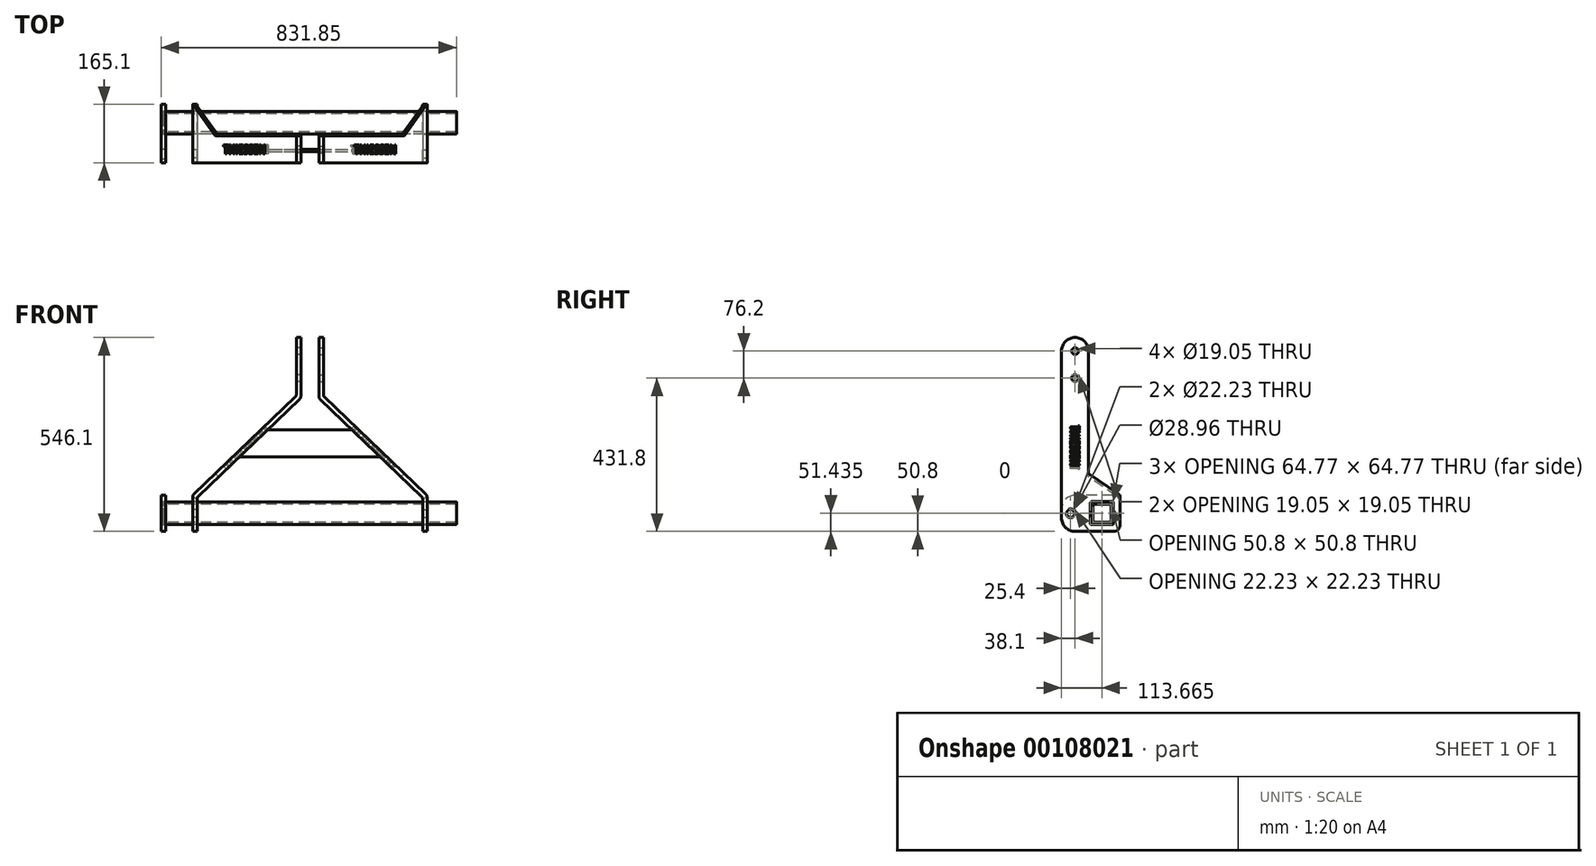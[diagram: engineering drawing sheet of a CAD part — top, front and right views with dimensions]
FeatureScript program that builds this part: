
annotation { "Feature Type Name" : "Feature", "Feature Type Description" : "" }
export const myFeature = defineFeature(function(context is Context, id is Id, definition is map)
    precondition{}
    {
        {
            var Q0;
            Q0=qCreatedBy(makeId("Front.planeOp"),FACE);
            var sketch = newSketch(context, id + "F0", { "sketchPlane" : qUnion([Q0])});
            skLineSegment(sketch, "E0", {"start": v(-330.2, 0) * mm, "end": v(-330.2, 101.6) * mm});
            skLineSegment(sketch, "E1", {"start": v(-330.2, 101.6) * mm, "end": v(-38.1, 381) * mm});
            skLineSegment(sketch, "E2", {"start": v(-38.1, 381) * mm, "end": v(-38.1, 546.1) * mm});
            skLineSegment(sketch, "E3", {"start": v(0, 0) * mm, "end": v(0, 360.93) * mm, "construction": true});
            skLineSegment(sketch, "E4.MirrorCS", {"start": v(38.1, 381) * mm, "end": v(38.1, 546.1) * mm});
            skLineSegment(sketch, "E5.MirrorCS", {"start": v(330.2, 101.6) * mm, "end": v(38.1, 381) * mm});
            skLineSegment(sketch, "E6.MirrorCS", {"start": v(330.2, 0) * mm, "end": v(330.2, 101.6) * mm});
            skSolve(sketch);
        }
        {
            var Q0;
            Q0=qCreatedBy(makeId("Top.planeOp"),FACE);
            var sketch = newSketch(context, id + "F1", { "sketchPlane" : qUnion([Q0])});
            skPoint(sketch, "E7.0", {"position": v(-330.2, 0) * mm});
            skPoint(sketch, "E7.1", {"position": v(330.2, 0) * mm});
            skLineSegment(sketch, "E8", {"start": v(-330.2, 38.1) * mm, "end": v(-330.2, -38.1) * mm});
            skLineSegment(sketch, "E9", {"start": v(0, 137.53) * mm, "end": v(0, -182.2) * mm, "construction": true});
            skLineSegment(sketch, "E10", {"start": v(-330.2, 38.1) * mm, "end": v(-317.5, 38.1) * mm});
            skLineSegment(sketch, "E11", {"start": v(-317.5, 38.1) * mm, "end": v(-317.5, -38.1) * mm});
            skLineSegment(sketch, "E12", {"start": v(-317.5, -38.1) * mm, "end": v(-330.2, -38.1) * mm});
            skSolve(sketch);
        }
        {
            var Q0;
            Q0=makeQuery(id+"F1.imprint","IMPRINT",FACE,{"disambiguationData":[TD([[makeQuery(id+"F1.imprint","IMPRINT",EDGE,{"derivedFrom":sQuery(id+"F1.wireOp",EDGE,"E8")}),1.0]])]});
            var Q1;
            Q1=sQuery(id+"F0.wireOp",EDGE,"E1");
            var Q2;
            Q2=sQuery(id+"F0.wireOp",EDGE,"E0");
            var Q3;
            Q3=sQuery(id+"F0.wireOp",EDGE,"E2");
            sweep(context, id + "F2", {"profiles" : qUnion([Q0]), "path" : qUnion([Q1, Q2, Q3])});
        }
        {
            var Q0;
            Q0=makeQuery(id+"F2.opSweep","SWEPT_FACE",FACE,{"disambiguationData":[OSD([sQuery(id+"F0.wireOp",EDGE,"E0"),sQuery(id+"F1.wireOp",EDGE,"E10")])]});
            var sketch = newSketch(context, id + "F3", { "sketchPlane" : qUnion([Q0])});
            skLineSegment(sketch, "E13.0", {"start": v(330.2, 101.6) * mm, "end": v(38.1, 381) * mm});
            skLineSegment(sketch, "E13.1", {"start": v(317.5, 96.17) * mm, "end": v(25.4, 375.57) * mm});
            skLineSegment(sketch, "E13.2", {"start": v(330.2, 0) * mm, "end": v(330.2, 101.6) * mm});
            skLineSegment(sketch, "E13.3", {"start": v(317.5, 0) * mm, "end": v(317.5, 96.17) * mm});
            skLineSegment(sketch, "E13.4", {"start": v(317.5, 0) * mm, "end": v(330.2, 0) * mm});
            skLineSegment(sketch, "E14", {"start": v(265.96, 163.05) * mm, "end": v(257.18, 153.87) * mm});
            skSolve(sketch);
        }
        {
            var Q0;
            {var subQ0=sQuery(id+"F3.wireOp",EDGE,"E13.2");Q0=makeQuery(id+"F3.imprint","IMPRINT",FACE,{"disambiguationData":[TD([[makeQuery(id+"F3.imprint","IMPRINT",EDGE,{"derivedFrom":subQ0}),1.0]])]});}
            extrude(context, id + "F4", {"entities" : qUnion([Q0]), "operationType" : NewBodyOperationType.ADD, "depth" : 88.9 * mm});
        }
        {
            var Q0;
            Q0=makeQuery(id+"F4.boolean.opBoolean","MERGE",FACE,{"derivedFrom":[makeQuery(id+"F2.opSweep","SWEPT_FACE",FACE,{"disambiguationData":[OSD([sQuery(id+"F0.wireOp",EDGE,"E1"),sQuery(id+"F1.wireOp",EDGE,"E8")])]}),makeQuery(id+"F4.opExtrude","SWEPT_FACE",FACE,{"disambiguationData":[OSD([sQuery(id+"F3.wireOp",EDGE,"E13.0")])]})]});
            var sketch = newSketch(context, id + "F5", { "sketchPlane" : qUnion([Q0])});
            skLineSegment(sketch, "E15.0", {"start": v(-79.49, 127) * mm, "end": v(-79.49, 38.1) * mm});
            skLineSegment(sketch, "E15.1", {"start": v(-168.39, 127) * mm, "end": v(-79.49, 127) * mm});
            skLineSegment(sketch, "E16", {"start": v(-79.49, 38.1) * mm, "end": v(-168.39, 127) * mm});
            skSolve(sketch);
        }
        {
            var Q0;
            Q0 = qSketchRegion(id + "F5", true);
            var Q1;
            Q1=makeQuery(id+"F4.boolean.opBoolean","MERGE",FACE,{"derivedFrom":[makeQuery(id+"F2.opSweep","SWEPT_FACE",FACE,{"disambiguationData":[OSD([sQuery(id+"F0.wireOp",EDGE,"E1"),sQuery(id+"F1.wireOp",EDGE,"E11")])]}),makeQuery(id+"F4.opExtrude","SWEPT_FACE",FACE,{"disambiguationData":[OSD([sQuery(id+"F3.wireOp",EDGE,"E13.1")])]})]});
            extrude(context, id + "F6", {"entities" : qUnion([Q0]), "operationType" : NewBodyOperationType.REMOVE, "endBound" : BoundingType.THROUGH_ALL, "oppositeDirection" : true, "endBoundEntityFace" : qUnion([Q1]), "depth" : 25.4 * mm});
        }
        {
            var Q0;
            Q0=makeQuery(id+"F2.opSweep","MID_CAP_EDGE",EDGE,{"disambiguationData":[OSD([sQuery(id+"F0.wireOp",VERTEX,"E0.end"),sQuery(id+"F1.wireOp",EDGE,"E8")])],"capPos":1.0});
            var Q1;
            Q1=makeQuery(id+"F2.opSweep","MID_CAP_EDGE",EDGE,{"disambiguationData":[OSD([sQuery(id+"F0.wireOp",VERTEX,"E0.end"),sQuery(id+"F1.wireOp",EDGE,"E11")])],"capPos":1.0});
            var Q2;
            Q2=makeQuery(id+"F2.opSweep","MID_CAP_EDGE",EDGE,{"disambiguationData":[OSD([sQuery(id+"F0.wireOp",VERTEX,"E2.start"),sQuery(id+"F1.wireOp",EDGE,"E8")])],"capPos":2.0});
            var Q3;
            Q3=makeQuery(id+"F2.opSweep","MID_CAP_EDGE",EDGE,{"disambiguationData":[OSD([sQuery(id+"F0.wireOp",VERTEX,"E2.start"),sQuery(id+"F1.wireOp",EDGE,"E11")])],"capPos":2.0});
            fillet(context, id + "F7", {"entities" : qUnion([Q0, Q1, Q2, Q3]), "radius" : 12.7 * mm, "tangentPropagation" : true, "allowEdgeOverflow" : false});
        }
        {
            var Q0;
            Q0=makeQuery(id+"F2.opSweep","CAP_EDGE",EDGE,{"disambiguationData":[OSD([sQuery(id+"F0.wireOp",VERTEX,"E2.end"),sQuery(id+"F1.wireOp",EDGE,"E12")])],"isStart":false});
            var Q1;
            Q1=makeQuery(id+"F2.opSweep","CAP_EDGE",EDGE,{"disambiguationData":[OSD([sQuery(id+"F0.wireOp",VERTEX,"E2.end"),sQuery(id+"F1.wireOp",EDGE,"E10")])],"isStart":false});
            var Q2;
            Q2=makeQuery(id+"F2.opSweep","CAP_EDGE",EDGE,{"disambiguationData":[OSD([sQuery(id+"F0.wireOp",VERTEX,"E0.start"),sQuery(id+"F1.wireOp",EDGE,"E12")])],"isStart":true});
            fillet(context, id + "F8", {"entities" : qUnion([Q0, Q1, Q2]), "radius" : 38.1 * mm, "tangentPropagation" : true, "allowEdgeOverflow" : false});
        }
        {
            var Q0;
            Q0=makeQuery(id+"F2.opSweep","SWEPT_FACE",FACE,{"disambiguationData":[OSD([sQuery(id+"F0.wireOp",EDGE,"E2"),sQuery(id+"F1.wireOp",EDGE,"E8")])]});
            var sketch = newSketch(context, id + "F9", { "sketchPlane" : qUnion([Q0])});
            skPoint(sketch, "E17.0", {"position": v(0, 546.1) * mm});
            skPoint(sketch, "E17.1", {"position": v(0, 381) * mm});
            skCircle(sketch, "E18", {"center": v(0, 508) * mm, "radius": 9.53 * mm});
            skCircle(sketch, "E19", {"center": v(0, 431.8) * mm, "radius": 9.53 * mm});
            skSolve(sketch);
        }
        {
            var Q0;
            Q0=makeQuery(id+"F9.imprint","IMPRINT",FACE,{"disambiguationData":[TD([[makeQuery(id+"F9.imprint","IMPRINT",EDGE,{"derivedFrom":sQuery(id+"F9.wireOp",EDGE,"E18")}),1.0]])]});
            var Q1;
            Q1=makeQuery(id+"F9.imprint","IMPRINT",FACE,{"disambiguationData":[TD([[makeQuery(id+"F9.imprint","IMPRINT",EDGE,{"derivedFrom":sQuery(id+"F9.wireOp",EDGE,"E19")}),1.0]])]});
            var Q2;
            Q2=makeQuery(id+"F2.opSweep","SWEPT_FACE",FACE,{"disambiguationData":[OSD([sQuery(id+"F0.wireOp",EDGE,"E2"),sQuery(id+"F1.wireOp",EDGE,"E11")])]});
            extrude(context, id + "F10", {"entities" : qUnion([Q0, Q1]), "operationType" : NewBodyOperationType.REMOVE, "endBound" : BoundingType.UP_TO_SURFACE, "oppositeDirection" : true, "endBoundEntityFace" : qUnion([Q2]), "depth" : 25.4 * mm});
        }
        {
            var Q0;
            Q0=makeQuery(id+"F2.opSweep","SWEPT_FACE",FACE,{"disambiguationData":[OSD([sQuery(id+"F0.wireOp",EDGE,"E0"),sQuery(id+"F1.wireOp",EDGE,"E8")])]});
            var sketch = newSketch(context, id + "F11", { "sketchPlane" : qUnion([Q0])});
            skPoint(sketch, "E20.0", {"position": v(0, 101.6) * mm});
            skPoint(sketch, "E20.1", {"position": v(0, 0) * mm});
            skCircle(sketch, "E21", {"center": v(12.7, 50.8) * mm, "radius": 11.11 * mm});
            skLineSegment(sketch, "E22.0", {"start": v(38.1, 38.1) * mm, "end": v(38.1, 96.17) * mm});
            skSolve(sketch);
        }
        {
            var Q0;
            Q0=makeQuery(id+"F11.imprint","IMPRINT",FACE,{"disambiguationData":[TD([[makeQuery(id+"F11.imprint","IMPRINT",EDGE,{"derivedFrom":sQuery(id+"F11.wireOp",EDGE,"E21")}),1.0]])]});
            var Q1;
            Q1=makeQuery(id+"F2.opSweep","SWEPT_FACE",FACE,{"disambiguationData":[OSD([sQuery(id+"F0.wireOp",EDGE,"E0"),sQuery(id+"F1.wireOp",EDGE,"E11")])]});
            extrude(context, id + "F12", {"entities" : qUnion([Q0]), "operationType" : NewBodyOperationType.REMOVE, "endBound" : BoundingType.UP_TO_SURFACE, "oppositeDirection" : true, "endBoundEntityFace" : qUnion([Q1]), "depth" : 25.4 * mm});
        }
        {
            var Q0;
            Q0=makeQuery(id+"F4.opExtrude","CAP_EDGE",EDGE,{"disambiguationData":[OSD([sQuery(id+"F3.wireOp",EDGE,"E13.4")])],"isStart":false});
            var Q1;
            Q1=makeQuery(id+"F6.boolean.opBoolean","COPY",EDGE,{"derivedFrom":makeQuery(id+"F6.opExtrude","SWEPT_EDGE",EDGE,{"disambiguationData":[OSD([sQuery(id+"F0.wireOp",VERTEX,"E0.end"),sQuery(id+"F1.wireOp",EDGE,"E8"),sQuery(id+"F3.wireOp",EDGE,"E13.0"),sQuery(id+"F3.wireOp",EDGE,"E13.2"),sQuery(id+"F5.wireOp",EDGE,"E15.1"),sQuery(id+"F5.wireOp",EDGE,"E16")])]})});
            var Q2;
            Q2=makeQuery(id+"F6.boolean.opBoolean","MERGE",EDGE,{"derivedFrom":[makeQuery(id+"F4.opExtrude","CAP_EDGE",EDGE,{"disambiguationData":[OSD([sQuery(id+"F3.wireOp",EDGE,"E14")])],"isStart":true}),makeQuery(id+"F6.opExtrude","SWEPT_EDGE",EDGE,{"disambiguationData":[OSD([sQuery(id+"F0.wireOp",EDGE,"E1"),sQuery(id+"F1.wireOp",EDGE,"E8"),sQuery(id+"F1.wireOp",EDGE,"E10"),sQuery(id+"F5.wireOp",EDGE,"E15.0"),sQuery(id+"F5.wireOp",EDGE,"E16")])]})]});
            fillet(context, id + "F13", {"entities" : qUnion([Q0, Q1, Q2]), "radius" : 19.05 * mm, "tangentPropagation" : true, "allowEdgeOverflow" : false});
        }
        {
            var Q0;
            Q0=makeQuery(id+"F4.boolean.opBoolean","MERGE",FACE,{"derivedFrom":[makeQuery(id+"F2.opSweep","SWEPT_FACE",FACE,{"disambiguationData":[OSD([sQuery(id+"F0.wireOp",EDGE,"E0"),sQuery(id+"F1.wireOp",EDGE,"E8")])]}),makeQuery(id+"F4.opExtrude","SWEPT_FACE",FACE,{"disambiguationData":[OSD([sQuery(id+"F3.wireOp",EDGE,"E13.2")])]})]});
            var sketch = newSketch(context, id + "F14", { "sketchPlane" : qUnion([Q0])});
            skLineSegment(sketch, "E23.0", {"start": v(-127, 19.05) * mm, "end": v(-127, 90.18) * mm});
            skLineSegment(sketch, "E23.1", {"start": v(-107.95, 0) * mm, "end": v(0, 0) * mm});
            skLineSegment(sketch, "E24", {"start": v(-107.95, 83.82) * mm, "end": v(-107.95, 19.05) * mm});
            skLineSegment(sketch, "E25", {"start": v(-107.95, 19.05) * mm, "end": v(-43.18, 19.05) * mm});
            skLineSegment(sketch, "E26", {"start": v(-43.18, 19.05) * mm, "end": v(-43.18, 83.82) * mm});
            skLineSegment(sketch, "E27", {"start": v(-43.18, 83.82) * mm, "end": v(-107.95, 83.82) * mm});
            skSolve(sketch);
        }
        {
            var Q0;
            Q0 = qSketchRegion(id + "F14", true);
            var Q1;
            Q1=makeQuery(id+"F4.boolean.opBoolean","MERGE",FACE,{"derivedFrom":[makeQuery(id+"F2.opSweep","SWEPT_FACE",FACE,{"disambiguationData":[OSD([sQuery(id+"F0.wireOp",EDGE,"E0"),sQuery(id+"F1.wireOp",EDGE,"E11")])]}),makeQuery(id+"F4.opExtrude","SWEPT_FACE",FACE,{"disambiguationData":[OSD([sQuery(id+"F3.wireOp",EDGE,"E13.3")])]})]});
            extrude(context, id + "F15", {"entities" : qUnion([Q0]), "operationType" : NewBodyOperationType.REMOVE, "endBound" : BoundingType.UP_TO_SURFACE, "oppositeDirection" : true, "endBoundEntityFace" : qUnion([Q1]), "depth" : 25.4 * mm});
        }
        {
            var Q0;
            Q0=makeQuery(id+"F15.boolean.opBoolean","COPY",EDGE,{"derivedFrom":makeQuery(id+"F15.opExtrude","SWEPT_EDGE",EDGE,{"disambiguationData":[OSD([sQuery(id+"F14.wireOp",EDGE,"E24"),sQuery(id+"F14.wireOp",EDGE,"E27")])]})});
            var Q1;
            Q1=makeQuery(id+"F15.boolean.opBoolean","COPY",EDGE,{"derivedFrom":makeQuery(id+"F15.opExtrude","SWEPT_EDGE",EDGE,{"disambiguationData":[OSD([sQuery(id+"F14.wireOp",EDGE,"E26"),sQuery(id+"F14.wireOp",EDGE,"E27")])]})});
            var Q2;
            Q2=makeQuery(id+"F15.boolean.opBoolean","COPY",EDGE,{"derivedFrom":makeQuery(id+"F15.opExtrude","SWEPT_EDGE",EDGE,{"disambiguationData":[OSD([sQuery(id+"F14.wireOp",EDGE,"E25"),sQuery(id+"F14.wireOp",EDGE,"E26")])]})});
            var Q3;
            Q3=makeQuery(id+"F15.boolean.opBoolean","COPY",EDGE,{"derivedFrom":makeQuery(id+"F15.opExtrude","SWEPT_EDGE",EDGE,{"disambiguationData":[OSD([sQuery(id+"F14.wireOp",EDGE,"E24"),sQuery(id+"F14.wireOp",EDGE,"E25")])]})});
            fillet(context, id + "F16", {"entities" : qUnion([Q0, Q1, Q2, Q3]), "radius" : 3.17 * mm, "tangentPropagation" : true, "allowEdgeOverflow" : false});
        }
        {
            var Q0;
            Q0=makeQuery(id+"F2.opSweep","SWEPT_BODY",BODY,{"disambiguationData":[OSD([sQuery(id+"F0.wireOp",EDGE,"E0"),sQuery(id+"F1.wireOp",EDGE,"E8"),sQuery(id+"F1.wireOp",EDGE,"E10"),sQuery(id+"F1.wireOp",EDGE,"E11"),sQuery(id+"F1.wireOp",EDGE,"E12")])]});
            var Q1;
            Q1=qCreatedBy(makeId("Right.planeOp"),FACE);
            mirror(context, id + "F17", {"entities" : qUnion([Q0]), "mirrorPlane" : qUnion([Q1])});
        }
        {
            var Q0;
            Q0=qCreatedBy(makeId("Right.planeOp"),FACE);
            var sketch = newSketch(context, id + "F18", { "sketchPlane" : qUnion([Q0])});
            skLineSegment(sketch, "E28.0", {"start": v(46.35, 83.82) * mm, "end": v(104.77, 83.82) * mm, "construction": true});
            skLineSegment(sketch, "E28.1", {"start": v(107.95, 80.65) * mm, "end": v(107.95, 22.22) * mm, "construction": true});
            skLineSegment(sketch, "E28.2", {"start": v(104.77, 19.05) * mm, "end": v(46.35, 19.05) * mm, "construction": true});
            skLineSegment(sketch, "E28.3", {"start": v(43.18, 22.22) * mm, "end": v(43.18, 80.65) * mm, "construction": true});
            skLineSegment(sketch, "E29", {"start": v(75.56, 83.82) * mm, "end": v(75.56, 19.05) * mm, "construction": true});
            skLineSegment(sketch, "E30", {"start": v(107.95, 51.44) * mm, "end": v(43.18, 51.44) * mm, "construction": true});
            skLineSegment(sketch, "E31", {"start": v(107.32, 83.19) * mm, "end": v(43.81, 83.19) * mm});
            skLineSegment(sketch, "E32", {"start": v(43.81, 83.19) * mm, "end": v(43.81, 19.69) * mm});
            skLineSegment(sketch, "E33", {"start": v(43.81, 19.69) * mm, "end": v(107.31, 19.69) * mm});
            skLineSegment(sketch, "E34", {"start": v(107.31, 19.69) * mm, "end": v(107.31, 83.18) * mm});
            skLineSegment(sketch, "E35", {"start": v(100.96, 76.84) * mm, "end": v(50.16, 76.84) * mm});
            skLineSegment(sketch, "E36", {"start": v(50.16, 76.84) * mm, "end": v(50.16, 26.04) * mm});
            skLineSegment(sketch, "E37", {"start": v(50.16, 26.04) * mm, "end": v(100.96, 26.04) * mm});
            skLineSegment(sketch, "E38", {"start": v(100.96, 26.04) * mm, "end": v(100.96, 76.84) * mm});
            skSolve(sketch);
        }
        {
            var Q0;
            Q0=makeQuery(id+"F18.imprint","IMPRINT",FACE,{"disambiguationData":[TD([[makeQuery(id+"F18.imprint","IMPRINT",EDGE,{"derivedFrom":sQuery(id+"F18.wireOp",EDGE,"E31")}),1.0]])]});
            extrude(context, id + "F19", {"entities" : qUnion([Q0]), "endBound" : BoundingType.SYMMETRIC, "depth" : 825.5 * mm});
        }
        {
            var Q0;
            Q0=makeQuery(id+"F19.opExtrude","SWEPT_EDGE",EDGE,{"disambiguationData":[OSD([sQuery(id+"F18.wireOp",EDGE,"E35"),sQuery(id+"F18.wireOp",EDGE,"E38")])]});
            var Q1;
            Q1=makeQuery(id+"F19.opExtrude","SWEPT_EDGE",EDGE,{"disambiguationData":[OSD([sQuery(id+"F18.wireOp",EDGE,"E35"),sQuery(id+"F18.wireOp",EDGE,"E36")])]});
            var Q2;
            Q2=makeQuery(id+"F19.opExtrude","SWEPT_EDGE",EDGE,{"disambiguationData":[OSD([sQuery(id+"F18.wireOp",EDGE,"E36"),sQuery(id+"F18.wireOp",EDGE,"E37")])]});
            var Q3;
            Q3=makeQuery(id+"F19.opExtrude","SWEPT_EDGE",EDGE,{"disambiguationData":[OSD([sQuery(id+"F18.wireOp",EDGE,"E37"),sQuery(id+"F18.wireOp",EDGE,"E38")])]});
            var Q4;
            Q4=makeQuery(id+"F19.opExtrude","SWEPT_EDGE",EDGE,{"disambiguationData":[OSD([sQuery(id+"F18.wireOp",EDGE,"E31"),sQuery(id+"F18.wireOp",EDGE,"E32")])]});
            var Q5;
            Q5=makeQuery(id+"F19.opExtrude","SWEPT_EDGE",EDGE,{"disambiguationData":[OSD([sQuery(id+"F18.wireOp",EDGE,"E32"),sQuery(id+"F18.wireOp",EDGE,"E33")])]});
            var Q6;
            Q6=makeQuery(id+"F19.opExtrude","SWEPT_EDGE",EDGE,{"disambiguationData":[OSD([sQuery(id+"F18.wireOp",EDGE,"E33"),sQuery(id+"F18.wireOp",EDGE,"E34")])]});
            var Q7;
            Q7=makeQuery(id+"F19.opExtrude","SWEPT_EDGE",EDGE,{"disambiguationData":[OSD([sQuery(id+"F18.wireOp",EDGE,"E31"),sQuery(id+"F18.wireOp",EDGE,"E34")])]});
            fillet(context, id + "F20", {"entities" : qUnion([Q0, Q1, Q2, Q3, Q4, Q5, Q6, Q7]), "radius" : 6.35 * mm, "tangentPropagation" : true, "allowEdgeOverflow" : false});
        }
        {
            var Q0;
            Q0=makeQuery(id+"F4.boolean.opBoolean","MERGE",FACE,{"derivedFrom":[makeQuery(id+"F2.opSweep","SWEPT_FACE",FACE,{"disambiguationData":[OSD([sQuery(id+"F0.wireOp",EDGE,"E1"),sQuery(id+"F1.wireOp",EDGE,"E8")])]}),makeQuery(id+"F4.opExtrude","SWEPT_FACE",FACE,{"disambiguationData":[OSD([sQuery(id+"F3.wireOp",EDGE,"E13.0")])]})]});
            var sketch = newSketch(context, id + "F21", { "sketchPlane" : qUnion([Q0])});
            skText(sketch, "E39", { "text": "THIESSEN", "fontName": "OpenSans-Bold.ttf"});
            skLineSegment(sketch, "E40.0", {"start": v(230.4, -38.1) * mm, "end": v(230.4, 38.1) * mm});
            skLineSegment(sketch, "E40.1", {"start": v(-162.96, 121.57) * mm, "end": v(-162.96, -38.1) * mm});
            skLineSegment(sketch, "E40.2", {"start": v(-71.6, 38.1) * mm, "end": v(230.4, 38.1) * mm});
            skLineSegment(sketch, "E40.3", {"start": v(-162.96, -38.1) * mm, "end": v(230.4, -38.1) * mm});
            skLineSegment(sketch, "E41", {"start": v(230.4, 0) * mm, "end": v(-162.96, 0) * mm, "construction": true});
            skLineSegment(sketch, "E42", {"start": v(33.72, -38.1) * mm, "end": v(33.72, 38.1) * mm, "construction": true});
            const initialGuessF21  = {"E39": [-0.04892, -0.0127, 1, 0, 0.0254]};
            skSetInitialGuess(sketch, initialGuessF21);
            skSolve(sketch);
        }
        {
            var Q0;
            Q0=makeQuery(id+"F21.imprint","IMPRINT",FACE,{"disambiguationData":[TD([[makeQuery(id+"F21.imprint","IMPRINT",EDGE,{"derivedFrom":sQuery(id+"F21.wireOp",EDGE,"E39.sketch_text.stroke-104")}),-1.0]])]});
            var Q1;
            Q1=makeQuery(id+"F21.imprint","IMPRINT",FACE,{"disambiguationData":[TD([[makeQuery(id+"F21.imprint","IMPRINT",EDGE,{"derivedFrom":sQuery(id+"F21.wireOp",EDGE,"E39.sketch_text.stroke-92")}),-1.0]])]});
            var Q2;
            Q2=makeQuery(id+"F21.imprint","IMPRINT",FACE,{"disambiguationData":[TD([[makeQuery(id+"F21.imprint","IMPRINT",EDGE,{"derivedFrom":sQuery(id+"F21.wireOp",EDGE,"E39.sketch_text.stroke-64")}),-1.0]])]});
            var Q3;
            Q3=makeQuery(id+"F21.imprint","IMPRINT",FACE,{"disambiguationData":[TD([[makeQuery(id+"F21.imprint","IMPRINT",EDGE,{"derivedFrom":sQuery(id+"F21.wireOp",EDGE,"E39.sketch_text.stroke-36")}),-1.0]])]});
            var Q4;
            Q4=makeQuery(id+"F21.imprint","IMPRINT",FACE,{"disambiguationData":[TD([[makeQuery(id+"F21.imprint","IMPRINT",EDGE,{"derivedFrom":sQuery(id+"F21.wireOp",EDGE,"E39.sketch_text.stroke-24")}),-1.0]])]});
            var Q5;
            Q5=makeQuery(id+"F21.imprint","IMPRINT",FACE,{"disambiguationData":[TD([[makeQuery(id+"F21.imprint","IMPRINT",EDGE,{"derivedFrom":sQuery(id+"F21.wireOp",EDGE,"E39.sketch_text.stroke-20")}),-1.0]])]});
            var Q6;
            Q6=makeQuery(id+"F21.imprint","IMPRINT",FACE,{"disambiguationData":[TD([[makeQuery(id+"F21.imprint","IMPRINT",EDGE,{"derivedFrom":sQuery(id+"F21.wireOp",EDGE,"E39.sketch_text.stroke-8")}),-1.0]])]});
            var Q7;
            Q7=makeQuery(id+"F21.imprint","IMPRINT",FACE,{"disambiguationData":[TD([[makeQuery(id+"F21.imprint","IMPRINT",EDGE,{"derivedFrom":sQuery(id+"F21.wireOp",EDGE,"E39.sketch_text.stroke-0")}),-1.0]])]});
            var Q8;
            Q8=makeQuery(id+"F4.boolean.opBoolean","MERGE",FACE,{"derivedFrom":[makeQuery(id+"F2.opSweep","SWEPT_FACE",FACE,{"disambiguationData":[OSD([sQuery(id+"F0.wireOp",EDGE,"E1"),sQuery(id+"F1.wireOp",EDGE,"E11")])]}),makeQuery(id+"F4.opExtrude","SWEPT_FACE",FACE,{"disambiguationData":[OSD([sQuery(id+"F3.wireOp",EDGE,"E13.1")])]})]});
            extrude(context, id + "F22", {"entities" : qUnion([Q0, Q1, Q2, Q3, Q4, Q5, Q6, Q7]), "operationType" : NewBodyOperationType.REMOVE, "endBound" : BoundingType.UP_TO_SURFACE, "oppositeDirection" : true, "endBoundEntityFace" : qUnion([Q8]), "depth" : 25.4 * mm});
        }
        {
            var Q0;
            Q0=makeQuery(id+"F17.opPattern","COPY",FACE,{"derivedFrom":makeQuery(id+"F4.boolean.opBoolean","MERGE",FACE,{"derivedFrom":[makeQuery(id+"F2.opSweep","SWEPT_FACE",FACE,{"disambiguationData":[OSD([sQuery(id+"F0.wireOp",EDGE,"E1"),sQuery(id+"F1.wireOp",EDGE,"E8")])]}),makeQuery(id+"F4.opExtrude","SWEPT_FACE",FACE,{"disambiguationData":[OSD([sQuery(id+"F3.wireOp",EDGE,"E13.0")])]})]}),"instanceName":"1"});
            var sketch = newSketch(context, id + "F23", { "sketchPlane" : qUnion([Q0])});
            skLineSegment(sketch, "E43.0", {"start": v(-230.4, -38.1) * mm, "end": v(-230.4, 38.1) * mm});
            skLineSegment(sketch, "E43.1", {"start": v(162.96, 121.57) * mm, "end": v(162.96, -38.1) * mm});
            skLineSegment(sketch, "E43.2", {"start": v(162.96, -38.1) * mm, "end": v(-230.4, -38.1) * mm});
            skLineSegment(sketch, "E43.3", {"start": v(71.6, 38.1) * mm, "end": v(-230.4, 38.1) * mm});
            skText(sketch, "E44", { "text": "THIESSEN", "fontName": "OpenSans-Bold.ttf"});
            skLineSegment(sketch, "E45", {"start": v(-230.4, 0) * mm, "end": v(162.96, 0) * mm, "construction": true});
            skLineSegment(sketch, "E46", {"start": v(-33.72, -38.1) * mm, "end": v(-33.72, 38.1) * mm, "construction": true});
            const initialGuessF23  = {"E44": [-0.11635, -0.0127, 1, 0, 0.0254]};
            skSetInitialGuess(sketch, initialGuessF23);
            skSolve(sketch);
        }
        {
            var Q0;
            Q0=makeQuery(id+"F23.imprint","IMPRINT",FACE,{"disambiguationData":[TD([[makeQuery(id+"F23.imprint","IMPRINT",EDGE,{"derivedFrom":sQuery(id+"F23.wireOp",EDGE,"E44.sketch_text.stroke-0")}),-1.0]])]});
            var Q1;
            Q1=makeQuery(id+"F23.imprint","IMPRINT",FACE,{"disambiguationData":[TD([[makeQuery(id+"F23.imprint","IMPRINT",EDGE,{"derivedFrom":sQuery(id+"F23.wireOp",EDGE,"E44.sketch_text.stroke-8")}),-1.0]])]});
            var Q2;
            Q2=makeQuery(id+"F23.imprint","IMPRINT",FACE,{"disambiguationData":[TD([[makeQuery(id+"F23.imprint","IMPRINT",EDGE,{"derivedFrom":sQuery(id+"F23.wireOp",EDGE,"E44.sketch_text.stroke-20")}),-1.0]])]});
            var Q3;
            Q3=makeQuery(id+"F23.imprint","IMPRINT",FACE,{"disambiguationData":[TD([[makeQuery(id+"F23.imprint","IMPRINT",EDGE,{"derivedFrom":sQuery(id+"F23.wireOp",EDGE,"E44.sketch_text.stroke-24")}),-1.0]])]});
            var Q4;
            Q4=makeQuery(id+"F23.imprint","IMPRINT",FACE,{"disambiguationData":[TD([[makeQuery(id+"F23.imprint","IMPRINT",EDGE,{"derivedFrom":sQuery(id+"F23.wireOp",EDGE,"E44.sketch_text.stroke-36")}),-1.0]])]});
            var Q5;
            Q5=makeQuery(id+"F23.imprint","IMPRINT",FACE,{"disambiguationData":[TD([[makeQuery(id+"F23.imprint","IMPRINT",EDGE,{"derivedFrom":sQuery(id+"F23.wireOp",EDGE,"E44.sketch_text.stroke-64")}),-1.0]])]});
            var Q6;
            Q6=makeQuery(id+"F23.imprint","IMPRINT",FACE,{"disambiguationData":[TD([[makeQuery(id+"F23.imprint","IMPRINT",EDGE,{"derivedFrom":sQuery(id+"F23.wireOp",EDGE,"E44.sketch_text.stroke-92")}),-1.0]])]});
            var Q7;
            Q7=makeQuery(id+"F23.imprint","IMPRINT",FACE,{"disambiguationData":[TD([[makeQuery(id+"F23.imprint","IMPRINT",EDGE,{"derivedFrom":sQuery(id+"F23.wireOp",EDGE,"E44.sketch_text.stroke-104")}),-1.0]])]});
            var Q8;
            Q8=makeQuery(id+"F17.opPattern","COPY",FACE,{"derivedFrom":makeQuery(id+"F4.boolean.opBoolean","MERGE",FACE,{"derivedFrom":[makeQuery(id+"F2.opSweep","SWEPT_FACE",FACE,{"disambiguationData":[OSD([sQuery(id+"F0.wireOp",EDGE,"E1"),sQuery(id+"F1.wireOp",EDGE,"E11")])]}),makeQuery(id+"F4.opExtrude","SWEPT_FACE",FACE,{"disambiguationData":[OSD([sQuery(id+"F3.wireOp",EDGE,"E13.1")])]})]}),"instanceName":"1"});
            extrude(context, id + "F24", {"entities" : qUnion([Q0, Q1, Q2, Q3, Q4, Q5, Q6, Q7]), "operationType" : NewBodyOperationType.REMOVE, "endBound" : BoundingType.UP_TO_SURFACE, "oppositeDirection" : true, "endBoundEntityFace" : qUnion([Q8]), "depth" : 25.4 * mm});
        }
        {
            var Q0;
            Q0=makeQuery(id+"F4.boolean.opBoolean","MERGE",FACE,{"derivedFrom":[makeQuery(id+"F2.opSweep","SWEPT_FACE",FACE,{"disambiguationData":[OSD([sQuery(id+"F0.wireOp",EDGE,"E0"),sQuery(id+"F1.wireOp",EDGE,"E8")])]}),makeQuery(id+"F4.opExtrude","SWEPT_FACE",FACE,{"disambiguationData":[OSD([sQuery(id+"F3.wireOp",EDGE,"E13.2")])]})]});
            cPlane(context, id + "F25", {"entities" : qUnion([Q0]), "cplaneType" : CPlaneType.OFFSET, "offset" : 76.2 * mm, "width" : 152.4 * mm, "height" : 152.4 * mm});
        }
        {
            var Q0;
            Q0=qCreatedBy(id+"F25.planeOp",FACE);
            var sketch = newSketch(context, id + "F26", { "sketchPlane" : qUnion([Q0])});
            skArc(sketch, "E47.0", {"start": v(0, 0) * mm, "mid": v(26.94, 11.16) * mm, "end": v(38.1, 38.1) * mm});
            skLineSegment(sketch, "E47.1", {"start": v(-107.95, 0) * mm, "end": v(0, 0) * mm});
            skArc(sketch, "E47.2", {"start": v(-127, 19.05) * mm, "mid": v(-121.42, 5.58) * mm, "end": v(-107.95, 0) * mm});
            skLineSegment(sketch, "E47.3", {"start": v(-127, 19.05) * mm, "end": v(-127, 82.55) * mm});
            skLineSegment(sketch, "E47.4", {"start": v(38.1, 38.1) * mm, "end": v(38.1, 63.5) * mm});
            skCircle(sketch, "E47.5", {"center": v(12.7, 50.8) * mm, "radius": 11.11 * mm, "construction": true});
            skArc(sketch, "E47.6", {"start": v(-107.95, 80.65) * mm, "mid": v(-107.02, 82.9) * mm, "end": v(-104.78, 83.82) * mm});
            skLineSegment(sketch, "E47.7", {"start": v(-46.36, 83.82) * mm, "end": v(-104.78, 83.82) * mm});
            skArc(sketch, "E47.8", {"start": v(-46.36, 83.82) * mm, "mid": v(-44.1, 82.9) * mm, "end": v(-43.18, 80.65) * mm});
            skLineSegment(sketch, "E47.9", {"start": v(-43.18, 22.22) * mm, "end": v(-43.18, 80.65) * mm});
            skLineSegment(sketch, "E47.10", {"start": v(-104.78, 19.05) * mm, "end": v(-46.36, 19.05) * mm});
            skArc(sketch, "E47.11", {"start": v(-43.18, 22.22) * mm, "mid": v(-44.1, 19.98) * mm, "end": v(-46.36, 19.05) * mm});
            skArc(sketch, "E47.12", {"start": v(-104.78, 19.05) * mm, "mid": v(-107.02, 19.98) * mm, "end": v(-107.95, 22.22) * mm});
            skLineSegment(sketch, "E47.13", {"start": v(-107.95, 80.65) * mm, "end": v(-107.95, 22.22) * mm});
            skLineSegment(sketch, "E48", {"start": v(12.7, 50.8) * mm, "end": v(-127, 50.8) * mm, "construction": true});
            skArc(sketch, "E49.MirrorCS", {"start": v(-127, 82.55) * mm, "mid": v(-121.42, 96.02) * mm, "end": v(-107.95, 101.6) * mm});
            skLineSegment(sketch, "E50.MirrorCS", {"start": v(-107.95, 101.6) * mm, "end": v(0, 101.6) * mm});
            skArc(sketch, "E51.MirrorCS", {"start": v(0, 101.6) * mm, "mid": v(26.94, 90.44) * mm, "end": v(38.1, 63.5) * mm});
            skPoint(sketch, "E52.orphan", {"position": v(-127, 90.18) * mm});
            skPoint(sketch, "E53.orphan", {"position": v(38.1, 96.17) * mm});
            skCircle(sketch, "E54", {"center": v(12.7, 50.8) * mm, "radius": 14.48 * mm});
            skSolve(sketch);
        }
        {
            var Q0;
            Q0=makeQuery(id+"F26.imprint","IMPRINT",FACE,{"disambiguationData":[TD([[makeQuery(id+"F26.imprint","IMPRINT",EDGE,{"derivedFrom":sQuery(id+"F26.wireOp",EDGE,"E47.0")}),1.0]])]});
            extrude(context, id + "F27", {"entities" : qUnion([Q0]), "depth" : 12.7 * mm});
        }
        {
            var Q0;
            Q0=qCreatedBy(makeId("Front.planeOp"),FACE);
            var sketch = newSketch(context, id + "F28", { "sketchPlane" : qUnion([Q0])});
            skLineSegment(sketch, "E55.0", {"start": v(-313.58, 99.92) * mm, "end": v(-29.32, 371.82) * mm});
            skLineSegment(sketch, "E55.1", {"start": v(313.58, 99.92) * mm, "end": v(29.32, 371.82) * mm});
            skLineSegment(sketch, "E55.2", {"start": v(-412.75, 83.19) * mm, "end": v(412.75, 83.19) * mm});
            skLineSegment(sketch, "E56", {"start": v(-118.64, 286.38) * mm, "end": v(118.64, 286.38) * mm});
            skLineSegment(sketch, "E57", {"start": v(-198.3, 210.18) * mm, "end": v(198.3, 210.18) * mm});
            skSolve(sketch);
        }
        {
            var Q0;
            {var subQ0=sQuery(id+"F28.wireOp",EDGE,"E56");Q0=makeQuery(id+"F28.imprint","IMPRINT",FACE,{"disambiguationData":[TD([[makeQuery(id+"F28.imprint","IMPRINT",EDGE,{"derivedFrom":subQ0}),-1.0]])]});}
            extrude(context, id + "F29", {"entities" : qUnion([Q0]), "depth" : 6.35 * mm});
        }
    });
